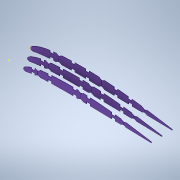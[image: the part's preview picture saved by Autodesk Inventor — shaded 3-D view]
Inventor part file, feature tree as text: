
AUTODESK INVENTOR PART (.ipt)
format: ipt  version: 2022 (Build 260153000, 153)  size: 1,030,144 bytes
history: native  units: mm
features: sketch x21, loft x4, plane x2, extrude x1
ambient origin geometry x8: Origin, YZ Plane, XZ Plane, XY Plane, X Axis, Y Axis, Z Axis, Center Point
bodies: Body1 (feature_tree)
feature tree (28):
  sketch  "Sketch3"  dims[d29=150.0mm d35=2.0mm]
  sketch  "Sketch4"  dims[d36=90.0deg d37=2.0mm]
  sketch  "Sketch5"  dims[d38=90.0deg d43=2.0mm]
  sketch  "Sketch6"  dims[d44=2.0mm d51=2.0mm]
  plane  "Work Plane2"
  sketch  "Sketch9"  dims[d52=2.0mm d56=2.0mm]
  sketch  "Sketch10"  dims[d57=2.0mm]
  sketch  "Sketch14"  dims[d65=2.0mm]
  sketch  "Sketch15"  dims[d66=2.0mm]
  sketch  "Sketch16"  dims[d69=2.0mm]
  sketch  "Sketch17"  dims[d70=2.0mm]
  sketch  "Sketch18"  dims[d76=2.0mm]
  sketch  "Sketch28"  dims[d77=0.0mm]
  sketch  "Sketch29"  dims[d150=1.8mm]
  sketch  "Sketch30"  dims[d151=1.8mm]
  sketch  "Sketch31"  dims[d156=1.8mm]
  sketch  "Sketch32"  dims[d157=1.8mm]
  sketch  "Sketch33"  dims[d167=1.8mm]
  sketch  "Sketch34"  dims[d168=90.0deg]
  sketch  "Sketch35"  dims[d169=1.8mm]
  loft  "Loft3"
  loft  "Loft4"
  loft  "Loft5"
  loft  "Loft6"
  plane  "Work Plane3"
  extrude  "Extrusion3"  Depth=2.0mm
  sketch  "Sketch37"  dims[d175=1.8mm d176=1.8mm d187=1.8mm d188=1.8mm d193=1.8mm d194=90.0deg d195=1.8mm d196=90.0deg d203=25.0mm d204=25.0mm d205=25.0mm d206=25.0mm d207=25.0mm d208=25.0mm d209=25.0mm d210=25.0mm d211=25.0mm d212=25.0mm d213=25.0mm d214=25.0mm d215=25.0mm d216=25.0mm d217=25.0mm d218=25.0mm d219=25.0mm d220=25.0mm d221=25.0mm d222=25.0mm d223=25.0mm d224=25.0mm d225=25.0mm d226=25.0mm d227=25.0mm d228=25.0mm d229=25.0mm d230=25.0mm d231=25.0mm d232=25.0mm d233=25.0mm d234=25.0mm d235=25.0mm d236=25.0mm d237=25.0mm d238=25.0mm d239=25.0mm d240=25.0mm d241=25.0mm d242=25.0mm d249=2.0mm d250=2.0mm d251=2.0mm d252=2.0mm d253=2.0mm d254=2.0mm d255=2.0mm d256=2.0mm d257=2.0mm d258=2.0mm d259=2.0mm d260=2.0mm d261=2.0mm d262=2.0mm d263=2.0mm d264=2.0mm d265=2.0mm d266=2.0mm d267=2.0mm d268=2.0mm d269=2.0mm d270=2.0mm d271=2.0mm d272=2.0mm d277=0.0mm d278=90.0deg d279=0.0mm d280=90.0deg d281=0.0mm d282=90.0deg d283=0.0mm d284=90.0deg d285=0.0mm d286=90.0deg d287=0.0mm d288=90.0deg d289=0.0mm d290=90.0deg d291=0.0mm d292=90.0deg d293=300.0mm d295=5000.0mm d296=2.0mm d297=5000.0mm d298=72.0mm d299=5000.0mm d300=2.0mm d301=5000.0mm d302=72.0mm d303=5000.0mm d304=0.0mm d6=0.5mm d7=0.872665mm d8=0.5mm d9=0.872665mm]
  sketch  "Sketch36"  dims[d170=90.0deg]
